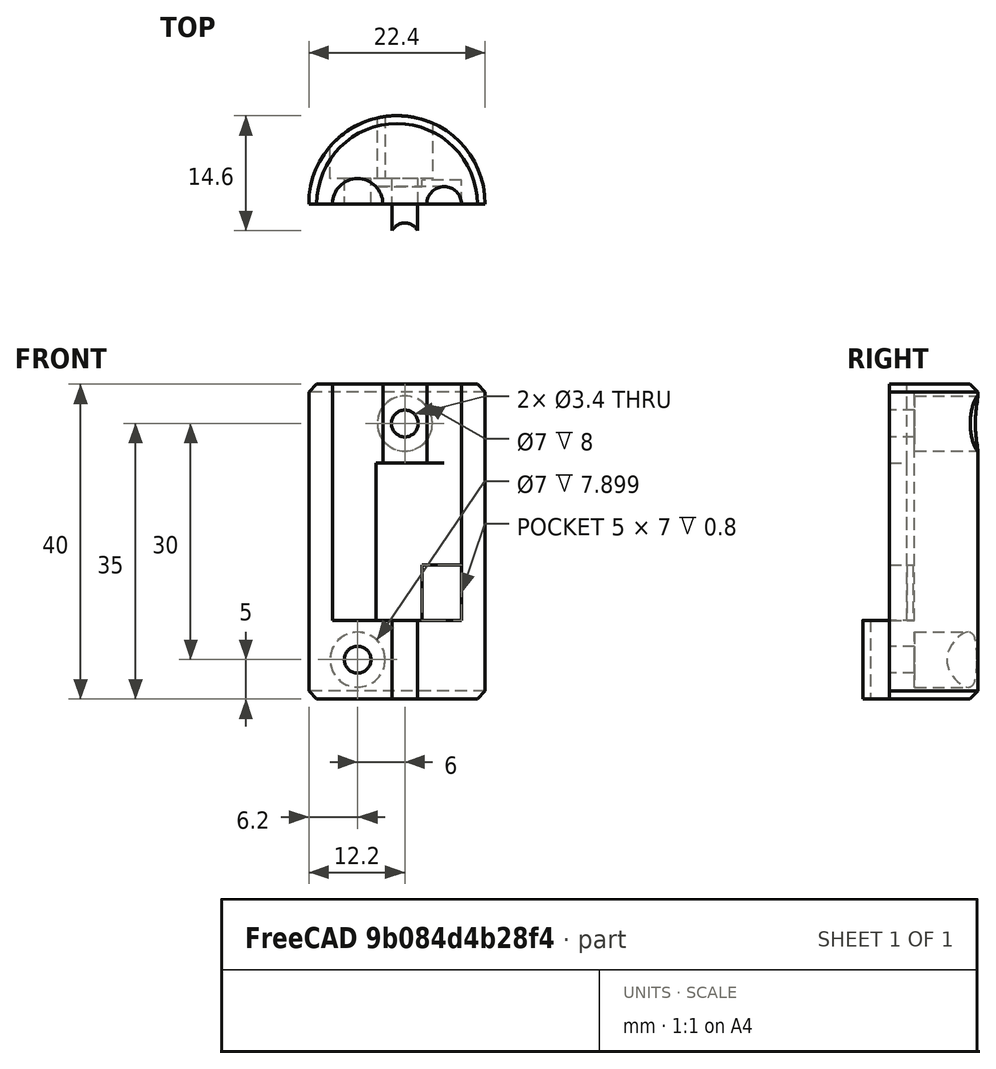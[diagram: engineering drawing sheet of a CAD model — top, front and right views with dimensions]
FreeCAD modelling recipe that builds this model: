
FCSTD DOCUMENT  (FreeCAD 0.21R33771 (Git))
Label: J-Pole_433_Bot1
Comment: J-Pole antenna bottom shell 1 (screwed part)
License: CC BY-SA 4.0 (SPDX-ID: CC-BY-SA-4.0)
LicenseURL: https://creativecommons.org/licenses/by-sa/4.0/legalcode.txt
objects: Sketcher::SketchObject×8, PartDesign::Pocket×6, PartDesign::Pad×2, PartDesign::Chamfer×1, PartDesign::Body×1, Mesh::Feature×1
note: 27 computed .brp shape members not serialized (recipe doc carries the construction recipe); baked Part::Feature solids carry a one-line shape summary decoded from their .brp

FEATURE [Sketcher::SketchObject] Sketch
  FullyConstrained = true
  MapMode = 5
  Support = -> [XY_Plane]
  sketch-geometry (2):
    g0: LineSegment StartX=-11.2 StartY=1.4e-15 StartZ=0 EndX=11.2 EndY=1.4e-15 EndZ=0
    g1: ArcOfCircle CenterX=0 CenterY=0 CenterZ=0 NormalX=0 NormalY=0 NormalZ=1 AngleXU=0 Radius=11.2 StartAngle=0 EndAngle=3.14159
  constraints (6):
    c: PointOnObject(g0,g-1)
    c: Horizontal(g0)
    c: Coincident(g1,g-1)
    c: Coincident(g1,g0)
    c: Coincident(g1,g0)
    c: Radius(g1) = 11.2
FEATURE [PartDesign::Pad] Pad
  Direction = (0,0,1)
  Length = 40
  Length2 = 10
  Profile = -> Sketch
  ReferenceAxis = -> Sketch [N_Axis]
  Type = 0
FEATURE [Sketcher::SketchObject] Sketch001
  ExternalGeometry = -> [Pad]
  FullyConstrained = true
  MapMode = 5
  Placement = pos=(0,0,40) rot=(0,0,1;0rad)
  Support = -> [Pad]
  sketch-geometry (2):
    g0: Circle CenterX=-5 CenterY=1.4e-15 CenterZ=0 NormalX=0 NormalY=0 NormalZ=1 AngleXU=0 Radius=3.2
    g1: Circle CenterX=6 CenterY=1.4e-15 CenterZ=0 NormalX=0 NormalY=0 NormalZ=1 AngleXU=0 Radius=2.2
  constraints (6):
    c: PointOnObject(g0,g-3)
    c: Radius(g0) = 3.2
    c: PointOnObject(g1,g-3)
    c: Radius(g1) = 2.2
    c: Distance(g-1,g0) = 5
    c: Distance(g-1,g1) = 6
FEATURE [PartDesign::Pocket] Pocket
  BaseFeature = -> Pad
  Direction = (0,0,-1)
  Length = 30
  Length2 = 5
  Profile = -> Sketch001
  ReferenceAxis = -> Sketch001 [N_Axis]
  Type = 0
FEATURE [Sketcher::SketchObject] Sketch002
  ExternalGeometry = -> [Pocket]
  FullyConstrained = true
  MapMode = 5
  Placement = pos=(0,1.4e-15,0) rot=(1,0,0;1.5708rad)
  Support = -> [Pocket]
  sketch-geometry (4):
    g0: LineSegment StartX=-5 StartY=10 StartZ=0 EndX=6 EndY=10 EndZ=0
    g1: LineSegment StartX=6 StartY=10 StartZ=0 EndX=6 EndY=30 EndZ=0
    g2: LineSegment StartX=6 StartY=30 StartZ=0 EndX=-5 EndY=30 EndZ=0
    g3: LineSegment StartX=-5 StartY=30 StartZ=0 EndX=-5 EndY=10 EndZ=0
  constraints (12):
    c: Coincident(g0,g1)
    c: Coincident(g1,g2)
    c: Coincident(g2,g3)
    c: Coincident(g3,g0)
    c: Horizontal(g2)
    c: Vertical(g1)
    c: Vertical(g3)
    c: DistanceY(g1,g1) = 20
    c: PointOnObject(g-3,g0)
    c: DistanceX(g-2,g0) = -5
    c: DistanceX(g-2,g0) = 6
    c: PointOnObject(g-4,g0)
FEATURE [PartDesign::Pocket] Pocket001
  BaseFeature = -> Pocket
  Direction = (0,1,-2e-16)
  Length = 2.2
  Length2 = 5
  Profile = -> Sketch002
  ReferenceAxis = -> Sketch002 [N_Axis]
  Type = 0
FEATURE [Sketcher::SketchObject] Sketch003
  ExternalGeometry = -> [Pocket001]
  FullyConstrained = true
  MapMode = 5
  Placement = pos=(0,1.4e-15,0) rot=(1,0,0;1.5708rad)
  Support = -> [Pocket001]
  sketch-geometry (4):
    g0: LineSegment StartX=-0.6 StartY=10 StartZ=0 EndX=2.6 EndY=10 EndZ=0
    g1: LineSegment StartX=2.6 StartY=10 StartZ=0 EndX=2.6 EndY=0 EndZ=0
    g2: LineSegment StartX=2.6 StartY=0 StartZ=0 EndX=-0.6 EndY=0 EndZ=0
    g3: LineSegment StartX=-0.6 StartY=0 StartZ=0 EndX=-0.6 EndY=10 EndZ=0
  constraints (12):
    c: Coincident(g0,g1)
    c: Coincident(g1,g2)
    c: Coincident(g2,g3)
    c: Coincident(g3,g0)
    c: Horizontal(g0)
    c: Horizontal(g2)
    c: Vertical(g1)
    c: Vertical(g3)
    c: PointOnObject(g0,g-3)
    c: PointOnObject(g1,g-1)
    c: DistanceX(g2,g2) = 3.2
    c: Distance(g-3,g0) = 1.2
FEATURE [PartDesign::Pad] Pad001
  BaseFeature = -> Pocket001
  Direction = (0,-1,2e-16)
  Length = 3.4
  Length2 = 10
  Profile = -> Sketch003
  ReferenceAxis = -> Sketch003 [N_Axis]
  Type = 0
FEATURE [Sketcher::SketchObject] Sketch004
  ExternalGeometry = -> [Pad001]
  FullyConstrained = true
  MapMode = 5
  Placement = pos=(0,1.4e-15,0) rot=(1,0,0;1.5708rad)
  Support = -> [Pad001]
  sketch-geometry (2):
    g0: Circle CenterX=1 CenterY=35 CenterZ=0 NormalX=0 NormalY=0 NormalZ=1 AngleXU=0 Radius=1.7
    g1: Circle CenterX=-5 CenterY=5 CenterZ=0 NormalX=0 NormalY=0 NormalZ=1 AngleXU=0 Radius=1.7
  constraints (6):
    c: DistanceY(g-1,g1) = 5
    c: DistanceX(g-2,g1) = -5
    c: Equal(g1,g0)
    c: Radius(g1) = 1.7
    c: DistanceX(g-2,g0) = 1
    c: Distance(g0,g-3) = 5
FEATURE [PartDesign::Pocket] Pocket002
  BaseFeature = -> Pad001
  Direction = (0,1,-2e-16)
  Length = 5
  Length2 = 5
  Profile = -> Sketch004
  ReferenceAxis = -> Sketch004 [N_Axis]
  Type = 1
FEATURE [Sketcher::SketchObject] Sketch005
  AttachmentOffset = pos=(0,0,-11.2) rot=(0,0,1;0rad)
  ExternalGeometry = -> [Pocket002]
  FullyConstrained = true
  MapMode = 5
  Placement = pos=(0,11.2,2.5e-15) rot=(1,0,0;1.5708rad)
  Support = -> [XZ_Plane]
  sketch-geometry (2):
    g0: Circle CenterX=-5 CenterY=5 CenterZ=0 NormalX=0 NormalY=0 NormalZ=1 AngleXU=0 Radius=3.5
    g1: Circle CenterX=1 CenterY=35 CenterZ=0 NormalX=0 NormalY=0 NormalZ=1 AngleXU=0 Radius=3.5
  constraints (6):
    c: DistanceX(g-2,g1) = 1
    c: DistanceX(g-2,g0) = -5
    c: DistanceY(g-1,g0) = 5
    c: Distance(g1,g-3) = 5
    c: Equal(g1,g0)
    c: Radius(g1) = 3.5
FEATURE [PartDesign::Pocket] Pocket003
  BaseFeature = -> Pocket002
  Direction = (0,1,2e-16)
  Length = 8
  Length2 = 5
  Profile = -> Sketch005
  ReferenceAxis = -> Sketch005 [N_Axis]
  Reversed = true
  Type = 0
FEATURE [Sketcher::SketchObject] Sketch006
  ExternalGeometry = -> [Pocket003]
  FullyConstrained = true
  MapMode = 5
  Placement = pos=(0,0,0) rot=(1,0,0;3.14159rad)
  Support = -> [Pocket003]
  sketch-geometry (1):
    g0: Circle CenterX=1.00237 CenterY=4.22 CenterZ=0 NormalX=0 NormalY=0 NormalZ=1 AngleXU=0 Radius=1.8
  constraints (3):
    c: Radius(g0) = 1.8
    c: PointOnObject(g-3,g0)
    c: Distance(g0,g-3) = 0.82
FEATURE [PartDesign::Pocket] Pocket004
  BaseFeature = -> Pocket003
  Direction = (0,2e-16,1)
  Length = 10
  Length2 = 5
  Profile = -> Sketch006
  ReferenceAxis = -> Sketch006 [N_Axis]
  Type = 0
FEATURE [Sketcher::SketchObject] Sketch007
  ExternalGeometry = -> [Pocket004]
  FullyConstrained = true
  MapMode = 5
  Placement = pos=(0,1.4e-15,0) rot=(1,0,0;1.5708rad)
  Support = -> [Pocket004]
  sketch-geometry (4):
    g0: LineSegment StartX=8.2 StartY=10 StartZ=0 EndX=3.2 EndY=10 EndZ=0
    g1: LineSegment StartX=3.2 StartY=10 StartZ=0 EndX=3.2 EndY=17 EndZ=0
    g2: LineSegment StartX=3.2 StartY=17 StartZ=0 EndX=8.2 EndY=17 EndZ=0
    g3: LineSegment StartX=8.2 StartY=17 StartZ=0 EndX=8.2 EndY=10 EndZ=0
  constraints (11):
    c: Coincident(g0,g1)
    c: Coincident(g1,g2)
    c: Coincident(g2,g3)
    c: Coincident(g3,g0)
    c: Horizontal(g0)
    c: Horizontal(g2)
    c: Vertical(g1)
    c: Vertical(g3)
    c: Coincident(g0,g-3)
    c: DistanceX(g2,g2) = 5
    c: DistanceY(g1,g1) = 7
FEATURE [PartDesign::Pocket] Pocket005
  BaseFeature = -> Pocket004
  Direction = (0,1,-2e-16)
  Length = 3
  Length2 = 5
  Profile = -> Sketch007
  ReferenceAxis = -> Sketch007 [N_Axis]
  Type = 0
FEATURE [PartDesign::Chamfer] Chamfer
  Angle = 45
  Base = -> Pocket005 [Edge14,Edge12]
  BaseFeature = -> Pocket005
  ChamferType = 0
  FlipDirection = false
  Size = 1
  Size2 = 1
  SupportTransform = false
  UseAllEdges = false
FEATURE [PartDesign::Body] Body
  Group = -> [Sketch,Pad,Sketch001,Pocket,Sketch002,Pocket001,Sketch003,Pad001,Sketch004,Pocket002,Sketch005,Pocket003,Sketch006,Pocket004,Sketch007,Pocket005,Chamfer]
  Origin = -> Origin
  Tip = -> Chamfer
FEATURE [Mesh::Feature] Mesh  label="J-Pole_433_Bot1"
